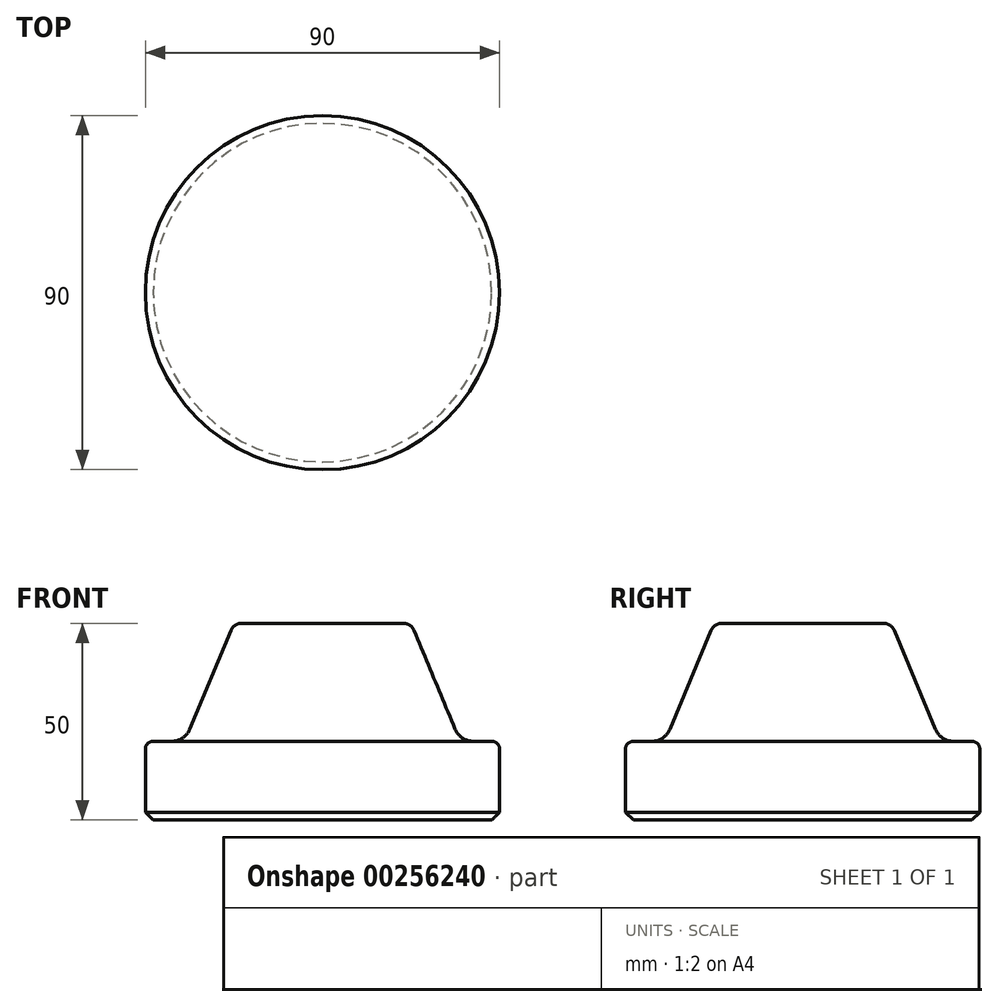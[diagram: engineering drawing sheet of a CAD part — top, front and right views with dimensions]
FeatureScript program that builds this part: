
annotation { "Feature Type Name" : "Feature", "Feature Type Description" : "" }
export const myFeature = defineFeature(function(context is Context, id is Id, definition is map)
    precondition{}
    {
        {
            var Q0;
            Q0=qCreatedBy(makeId("Front.planeOp"),FACE);
            var sketch = newSketch(context, id + "F0", { "sketchPlane" : qUnion([Q0])});
            skLineSegment(sketch, "E0", {"start": v(0, 50) * mm, "end": v(0, 0) * mm});
            skLineSegment(sketch, "E1", {"start": v(0, 0) * mm, "end": v(45, 0) * mm});
            skLineSegment(sketch, "E2", {"start": v(45, 0) * mm, "end": v(45, 18) * mm});
            skLineSegment(sketch, "E3", {"start": v(43, 20) * mm, "end": v(38.33, 20) * mm});
            skLineSegment(sketch, "E4", {"start": v(33.72, 23.08) * mm, "end": v(23.27, 48.15) * mm});
            skLineSegment(sketch, "E5", {"start": v(20.5, 50) * mm, "end": v(0, 50) * mm});
            skPoint(sketch, "E6.visualSharp", {"position": v(22.5, 50) * mm});
            skArc(sketch, "E6.filletArc", {"start": v(23.27, 48.15) * mm, "mid": v(22.16, 49.5) * mm, "end": v(20.5, 50) * mm});
            skPoint(sketch, "E7.visualSharp", {"position": v(35, 20) * mm});
            skArc(sketch, "E7.filletArc", {"start": v(33.72, 23.08) * mm, "mid": v(35.56, 20.84) * mm, "end": v(38.33, 20) * mm});
            skPoint(sketch, "E8.visualSharp", {"position": v(45, 20) * mm});
            skArc(sketch, "E8.filletArc", {"start": v(45, 18) * mm, "mid": v(44.41, 19.41) * mm, "end": v(43, 20) * mm});
            skLineSegment(sketch, "E9", {"start": v(0, 62.5) * mm, "end": v(0, -54.24) * mm, "construction": true});
            skPoint(sketch, "E9.endSnap0", {"position": v(0, 25) * mm});
            skSolve(sketch);
        }
        {
            var Q0;
            Q0=makeQuery(id+"F0.imprint","IMPRINT",FACE,{"disambiguationData":[TD([[makeQuery(id+"F0.imprint","IMPRINT",EDGE,{"derivedFrom":sQuery(id+"F0.wireOp",EDGE,"E0")}),1.0]])]});
            var Q1;
            Q1=sQuery(id+"F0.wireOp",EDGE,"E9");
            var Q2;
            Q2=sQuery(id+"F0.wireOp",EDGE,"E9");
            revolve(context, id + "F1", {"entities" : qUnion([Q0]), "surfaceEntities" : qUnion([Q1]), "axis" : qUnion([Q2]), "revolveType" : RevolveType.FULL});
        }
        {
            var Q0;
            Q0=makeQuery(id+"F1.opRevolve","SWEPT_EDGE",EDGE,{"disambiguationData":[OSD([sQuery(id+"F0.wireOp",EDGE,"E1"),sQuery(id+"F0.wireOp",EDGE,"E2")])]});
            chamfer(context, id + "F2", {"entities" : qUnion([Q0]), "width" : 2 * mm, "tangentPropagation" : true});
        }
    });
